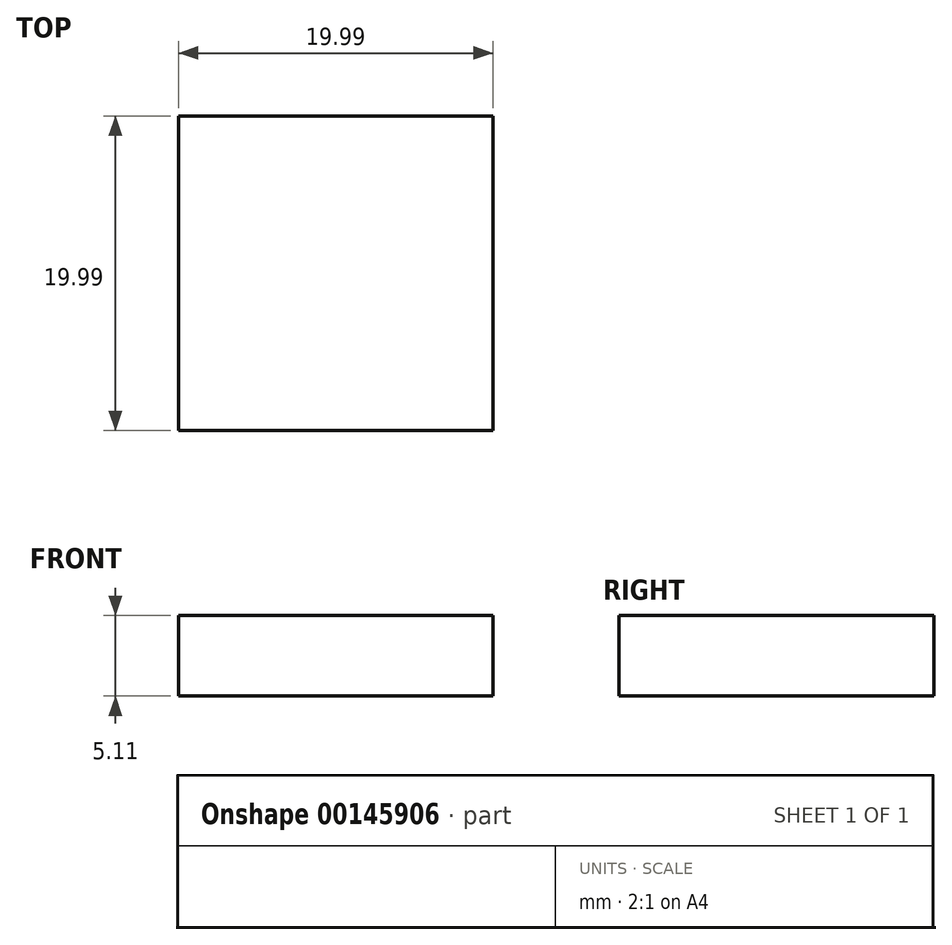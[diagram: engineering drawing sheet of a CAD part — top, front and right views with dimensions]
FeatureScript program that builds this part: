
annotation { "Feature Type Name" : "Feature", "Feature Type Description" : "" }
export const myFeature = defineFeature(function(context is Context, id is Id, definition is map)
    precondition{}
    {
        {
            var Q0;
            Q0=qCreatedBy(makeId("Top.planeOp"),FACE);
            var sketch = newSketch(context, id + "F0", { "sketchPlane" : qUnion([Q0])});
            skLineSegment(sketch, "E0.bottom", {"start": v(0, 0) * mm, "end": v(19.99, 0) * mm});
            skLineSegment(sketch, "E0.top", {"start": v(0, -19.99) * mm, "end": v(19.99, -19.99) * mm});
            skLineSegment(sketch, "E0.left", {"start": v(0, 0) * mm, "end": v(0, -19.99) * mm});
            skLineSegment(sketch, "E0.right", {"start": v(19.99, 0) * mm, "end": v(19.99, -19.99) * mm});
            skSolve(sketch);
        }
        {
            var Q0;
            Q0 = qSketchRegion(id + "F0", true);
            extrude(context, id + "F1", {"entities" : qUnion([Q0]), "depth" : 5.1 * mm});
        }
    });
